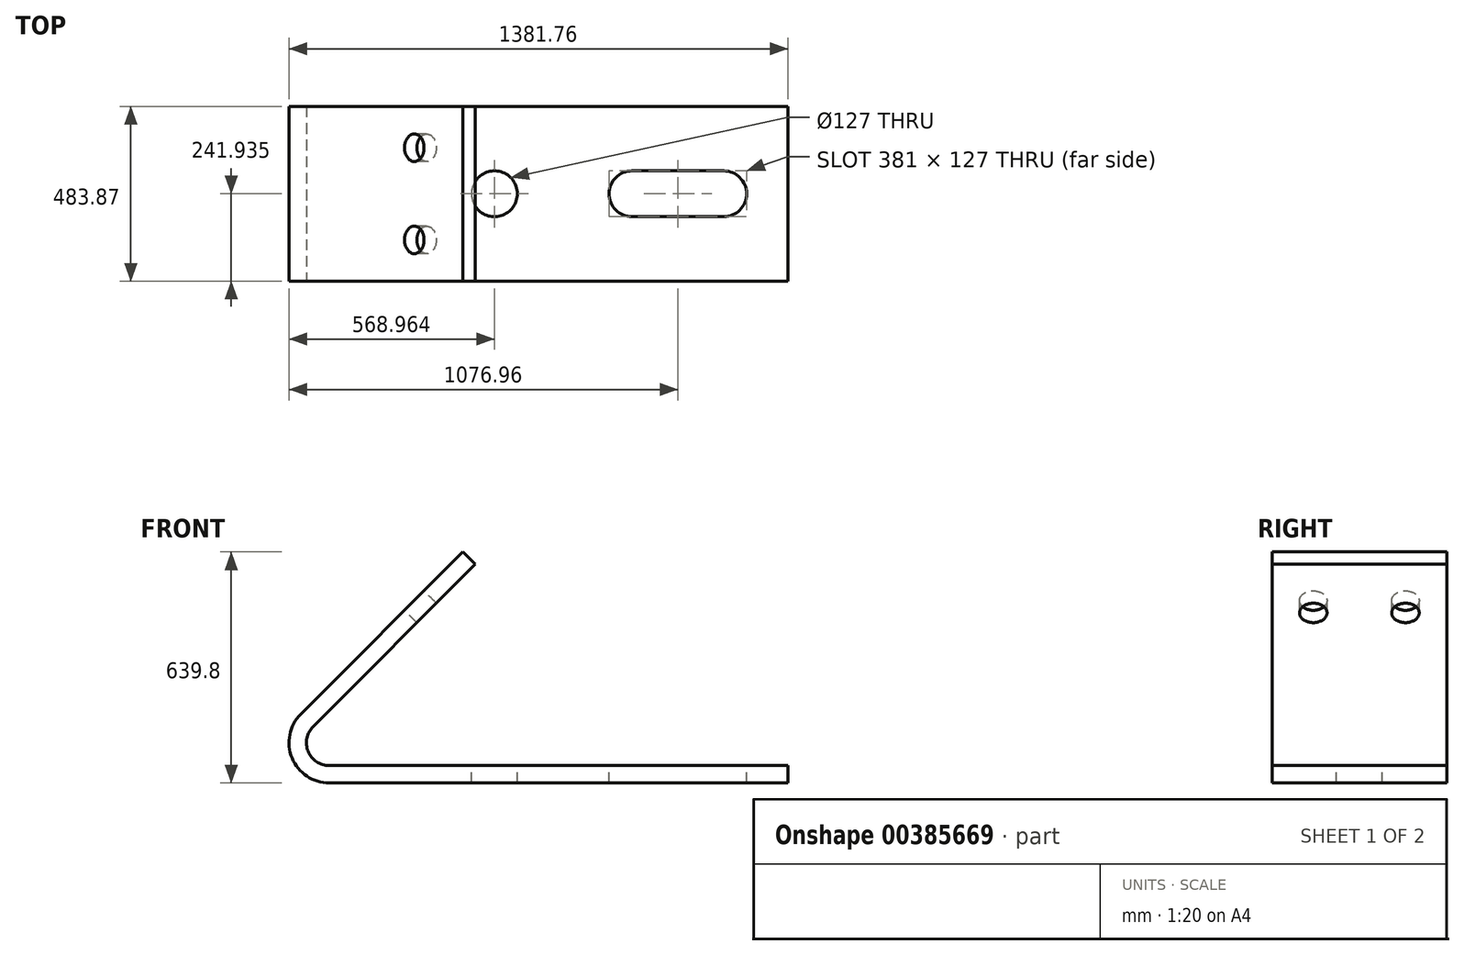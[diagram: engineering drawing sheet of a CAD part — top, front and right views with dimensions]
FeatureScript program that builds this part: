
annotation { "Feature Type Name" : "Feature", "Feature Type Description" : "" }
export const myFeature = defineFeature(function(context is Context, id is Id, definition is map)
    precondition{}
    {
        {
            var Q0;
            Q0=qCreatedBy(makeId("Front.planeOp"),FACE);
            var sketch = newSketch(context, id + "F0", { "sketchPlane" : qUnion([Q0])});
            skArc(sketch, "E0", {"start": v(-125.58, 190.79) * mm, "mid": v(-149.8, 69) * mm, "end": v(-46.56, 0) * mm});
            skLineSegment(sketch, "E1", {"start": v(-46.56, 0) * mm, "end": v(1223.44, 0) * mm});
            skPoint(sketch, "E2.orphan", {"position": v(-24.68, 0) * mm});
            skLineSegment(sketch, "E3", {"start": v(-125.58, 190.79) * mm, "end": v(323.43, 639.8) * mm});
            skLineSegment(sketch, "E4", {"start": v(1223.44, 0) * mm, "end": v(1223.44, 48.26) * mm});
            skLineSegment(sketch, "E5", {"start": v(323.43, 639.8) * mm, "end": v(357.56, 605.67) * mm});
            skLineSegment(sketch, "E6.0", {"start": v(-46.56, 48.26) * mm, "end": v(1223.44, 48.26) * mm});
            skArc(sketch, "E6.1", {"start": v(-91.46, 156.66) * mm, "mid": v(-105.22, 87.46) * mm, "end": v(-46.56, 48.26) * mm});
            skLineSegment(sketch, "E6.2", {"start": v(-91.46, 156.66) * mm, "end": v(357.56, 605.67) * mm});
            skSolve(sketch);
        }
        {
            var Q0;
            Q0=makeQuery(id+"F0.imprint","IMPRINT",FACE,{"disambiguationData":[TD([[makeQuery(id+"F0.imprint","IMPRINT",EDGE,{"derivedFrom":sQuery(id+"F0.wireOp",EDGE,"E0")}),1.0]])]});
            extrude(context, id + "F1", {"entities" : qUnion([Q0]), "oppositeDirection" : true, "depth" : 483.87 * mm});
        }
        {
            var Q0;
            Q0=makeQuery(id+"F1.opExtrude","SWEPT_FACE",FACE,{"disambiguationData":[OSD([sQuery(id+"F0.wireOp",EDGE,"E6.0")])]});
            var sketch = newSketch(context, id + "F2", { "sketchPlane" : qUnion([Q0])});
            skLineSegment(sketch, "E7.0", {"start": v(-46.56, 483.87) * mm, "end": v(1223.44, 483.87) * mm});
            skLineSegment(sketch, "E8.0", {"start": v(1223.44, 483.87) * mm, "end": v(1223.44, 0) * mm});
            skLineSegment(sketch, "E9.0.0", {"start": v(-46.56, 0) * mm, "end": v(1223.44, 0) * mm, "construction": true});
            skLineSegment(sketch, "E9.0.1", {"start": v(1223.44, 0) * mm, "end": v(1223.44, 483.87) * mm, "construction": true});
            skLineSegment(sketch, "E9.0.2", {"start": v(1223.44, 483.87) * mm, "end": v(-46.56, 483.87) * mm, "construction": true});
            skLineSegment(sketch, "E9.0.3", {"start": v(-46.56, 483.87) * mm, "end": v(-46.56, 0) * mm, "construction": true});
            skLineSegment(sketch, "E10", {"start": v(444.8, 241.93) * mm, "end": v(1438.36, 241.94) * mm, "construction": true});
            skArc(sketch, "E11", {"start": v(1045.64, 178.44) * mm, "mid": v(1109.14, 241.94) * mm, "end": v(1045.64, 305.44) * mm});
            skArc(sketch, "E12", {"start": v(791.64, 305.44) * mm, "mid": v(728.14, 241.94) * mm, "end": v(791.64, 178.44) * mm});
            skLineSegment(sketch, "E13", {"start": v(791.64, 178.43) * mm, "end": v(1045.64, 178.44) * mm});
            skLineSegment(sketch, "E14", {"start": v(791.64, 305.44) * mm, "end": v(1045.64, 305.44) * mm});
            skCircle(sketch, "E15", {"center": v(410.64, 241.93) * mm, "radius": 63.5 * mm});
            skSolve(sketch);
        }
        {
            var Q0;
            Q0=makeQuery(id+"F2.imprint","IMPRINT",FACE,{"disambiguationData":[TD([[makeQuery(id+"F2.imprint","IMPRINT",EDGE,{"derivedFrom":sQuery(id+"F2.wireOp",EDGE,"E11")}),1.0]])]});
            extrude(context, id + "F3", {"entities" : qUnion([Q0]), "operationType" : NewBodyOperationType.REMOVE, "oppositeDirection" : true, "depth" : 76.2 * mm});
        }
        {
            var Q0;
            Q0=makeQuery(id+"F1.opExtrude","SWEPT_FACE",FACE,{"disambiguationData":[OSD([sQuery(id+"F0.wireOp",EDGE,"E3")])]});
            var sketch = newSketch(context, id + "F4", { "sketchPlane" : qUnion([Q0])});
            skCircle(sketch, "E16", {"center": v(-369.57, 490.6) * mm, "radius": 38.1 * mm});
            skCircle(sketch, "E17", {"center": v(-114.3, 490.6) * mm, "radius": 38.1 * mm});
            skSolve(sketch);
        }
        {
            var Q0;
            Q0=makeQuery(id+"F4.imprint","IMPRINT",FACE,{"disambiguationData":[TD([[makeQuery(id+"F4.imprint","IMPRINT",EDGE,{"derivedFrom":sQuery(id+"F4.wireOp",EDGE,"E16")}),1.0]])]});
            var Q1;
            Q1=makeQuery(id+"F4.imprint","IMPRINT",FACE,{"disambiguationData":[TD([[makeQuery(id+"F4.imprint","IMPRINT",EDGE,{"derivedFrom":sQuery(id+"F4.wireOp",EDGE,"E17")}),1.0]])]});
            extrude(context, id + "F5", {"entities" : qUnion([Q0, Q1]), "operationType" : NewBodyOperationType.REMOVE, "oppositeDirection" : true, "depth" : 50.8 * mm});
        }
        {
            var Q0;
            Q0=makeQuery(id+"F2.imprint","IMPRINT",FACE,{"disambiguationData":[TD([[makeQuery(id+"F2.imprint","IMPRINT",EDGE,{"derivedFrom":sQuery(id+"F2.wireOp",EDGE,"E15")}),1.0]])]});
            extrude(context, id + "F6", {"entities" : qUnion([Q0]), "operationType" : NewBodyOperationType.REMOVE, "oppositeDirection" : true, "depth" : 50.8 * mm});
        }
    });
